# Revit family: Legrand boites de sol charge lourde FR
name_source: partatom
category: Installations électriques
units: mm (PartAtom-declared; Revit-internal decimal feet)

## family parameters
Conserver l'orientation des annotations = Non
Cote de connecteur circulaire = Utiliser le diamètre
Couper avec des vides une fois chargée = Non
Hôte = Face
Partagée = Non
Point de calcul de pièce = Non
Type d'élément = Normal

## types (3) — shared parameters
089686 = Frame : 089686
Fabricant = LEGRAND
Heavy = Charge : Charge lourde
Std = Charge : Charge standard
Type du sol = Charge : Charge standard
zero-valued in all types: Elévation par défaut

## per-type parameters (varying)
| type | 089685 | 089688 | Description | Frame | Supports |
| 24 modules sortie centrale | Frame : 089685 | Frame : 089688 | Charge lourde 24 modules avec sortie de câbles central | Frame : 089686 | 089686 |
| 24 modules sortie latérale | Frame : 089686 | Frame : 089686 | Charge lourde 24 modules avec sortie de câbles latérale | Frame : 089688 |  |
| Couvercle IP66 | Frame : 089686 | Frame : 089686 | Trappe d'accès charge lourde IP66 | Frame : 089685 |  |
